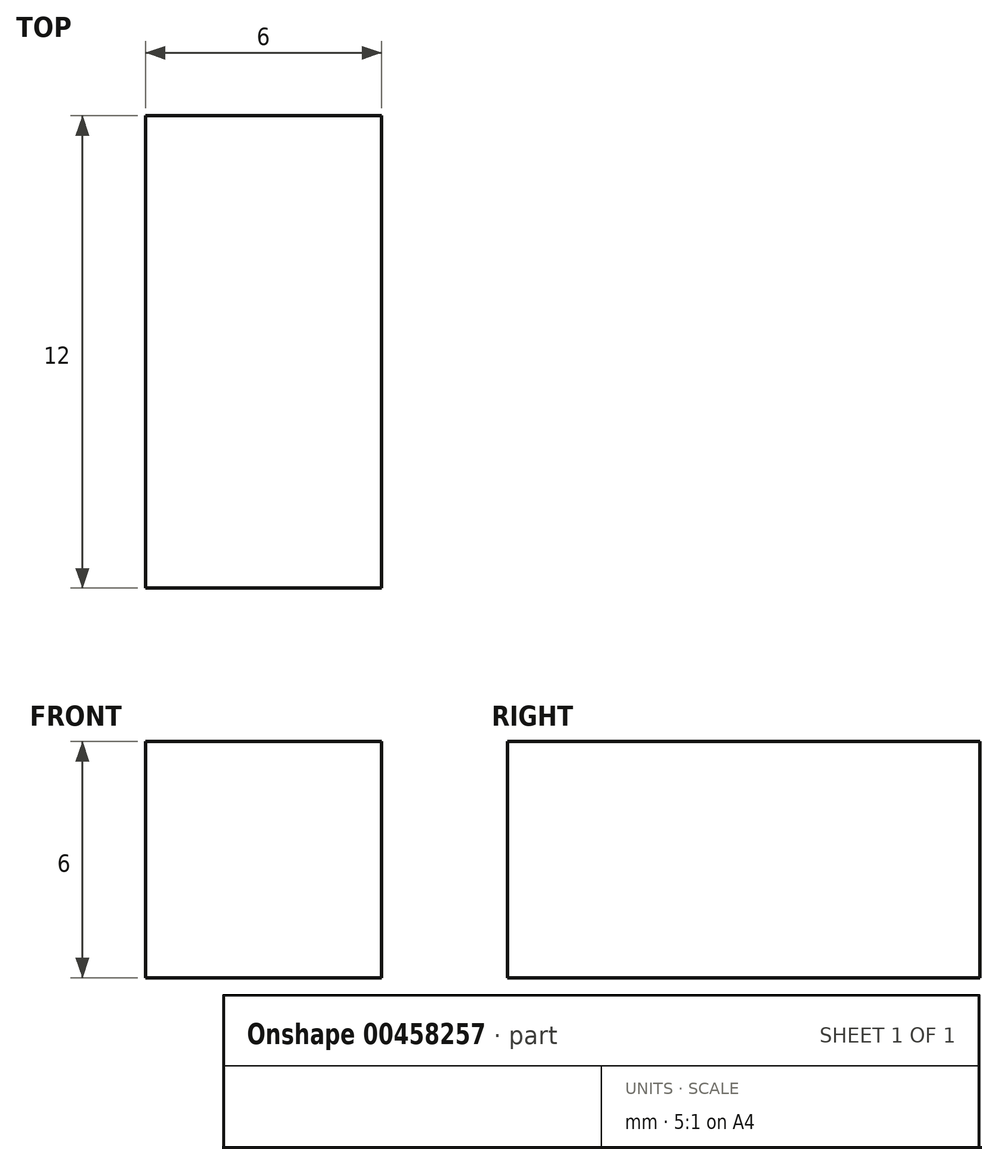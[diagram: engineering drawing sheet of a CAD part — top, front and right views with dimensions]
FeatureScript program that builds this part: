
annotation { "Feature Type Name" : "Feature", "Feature Type Description" : "" }
export const myFeature = defineFeature(function(context is Context, id is Id, definition is map)
    precondition{}
    {
        {
            var Q0;
            Q0=qCreatedBy(makeId("Front.planeOp"),FACE);
            var sketch = newSketch(context, id + "F0", { "sketchPlane" : qUnion([Q0])});
            skLineSegment(sketch, "E0.bottom", {"start": v(-3, 0) * mm, "end": v(3, 0) * mm});
            skLineSegment(sketch, "E0.top", {"start": v(-3, 6) * mm, "end": v(3, 6) * mm});
            skLineSegment(sketch, "E0.left", {"start": v(-3, 0) * mm, "end": v(-3, 6) * mm});
            skLineSegment(sketch, "E0.right", {"start": v(3, 0) * mm, "end": v(3, 6) * mm});
            skSolve(sketch);
        }
        {
            var Q0;
            Q0=makeQuery(id+"F0.imprint","IMPRINT",FACE,{"disambiguationData":[TD([[makeQuery(id+"F0.imprint","IMPRINT",EDGE,{"derivedFrom":sQuery(id+"F0.wireOp",EDGE,"E0.bottom")}),1.0]])]});
            extrude(context, id + "F1", {"entities" : qUnion([Q0]), "depth" : 12 * mm});
        }
    });
